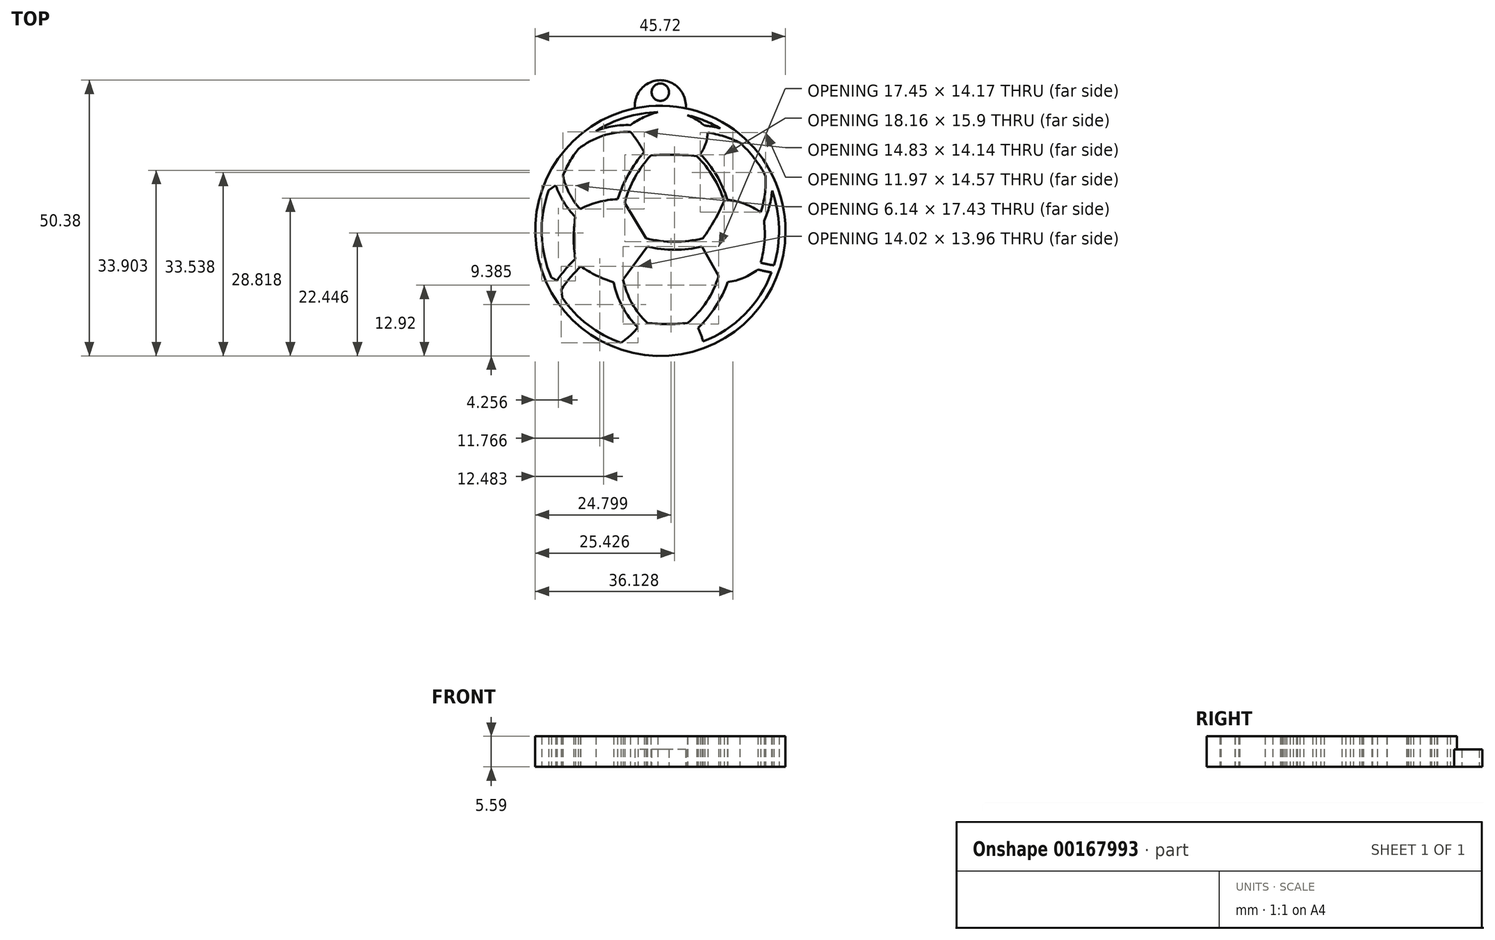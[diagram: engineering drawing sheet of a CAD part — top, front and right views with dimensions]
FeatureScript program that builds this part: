
annotation { "Feature Type Name" : "Feature", "Feature Type Description" : "" }
export const myFeature = defineFeature(function(context is Context, id is Id, definition is map)
    precondition{}
    {
        {
            var Q0;
            Q0=qCreatedBy(makeId("Top.planeOp"),FACE);
            var sketch = newSketch(context, id + "F0", { "sketchPlane" : qUnion([Q0])});
            skCircle(sketch, "E0", {"center": v(1.83, 6.23) * mm, "radius": 22.86 * mm});
            skPoint(sketch, "E0.centerSnap0", {"position": v(-21.03, 6.23) * mm});
            skPoint(sketch, "E0.centerSnap1", {"position": v(1.83, 29.1) * mm});
            skArc(sketch, "E1", {"start": v(9.64, -14) * mm, "mid": v(17.25, -9.02) * mm, "end": v(22.15, -1.36) * mm});
            skLineSegment(sketch, "E2", {"start": v(-18.54, 13.66) * mm, "end": v(-17.27, 14.53) * mm});
            skArc(sketch, "E3", {"start": v(-17.27, 14.53) * mm, "mid": v(-15.79, 11.46) * mm, "end": v(-13.7, 8.76) * mm});
            skArc(sketch, "E4", {"start": v(-13.15, 21.17) * mm, "mid": v(-14.73, 18.84) * mm, "end": v(-15.96, 16.3) * mm});
            skArc(sketch, "E5", {"start": v(-3.64, 25.54) * mm, "mid": v(-6.83, 25.35) * mm, "end": v(-9.9, 24.47) * mm});
            skArc(sketch, "E6", {"start": v(-3.64, 24.35) * mm, "mid": v(-8.67, 23.6) * mm, "end": v(-13.15, 21.17) * mm});
            skArc(sketch, "E7", {"start": v(-15.96, 16.3) * mm, "mid": v(-14.8, 13.05) * mm, "end": v(-12.82, 10.2) * mm});
            skArc(sketch, "E8", {"start": v(-5.97, 12.01) * mm, "mid": v(-9.5, 11.49) * mm, "end": v(-12.82, 10.2) * mm});
            skArc(sketch, "E9", {"start": v(-13.7, 8.76) * mm, "mid": v(-14, 4.92) * mm, "end": v(-13.7, 1.08) * mm});
            skArc(sketch, "E10", {"start": v(-13.7, 1.08) * mm, "mid": v(-15.51, -0.8) * mm, "end": v(-17.07, -2.9) * mm});
            skArc(sketch, "E11", {"start": v(-17.07, -2.9) * mm, "mid": v(-17.55, -2.57) * mm, "end": v(-18.08, -2.35) * mm});
            skArc(sketch, "E12", {"start": v(-16.1, -5.96) * mm, "mid": v(-16.15, -5.25) * mm, "end": v(-16.27, -4.55) * mm});
            skArc(sketch, "E13", {"start": v(-12.7, -0.26) * mm, "mid": v(-14.62, -2.3) * mm, "end": v(-16.27, -4.55) * mm});
            skArc(sketch, "E14", {"start": v(-12.7, -0.26) * mm, "mid": v(-9.8, -1.95) * mm, "end": v(-6.68, -3.16) * mm});
            skArc(sketch, "E15", {"start": v(-6.68, -3.16) * mm, "mid": v(-5.1, -7.64) * mm, "end": v(-2.25, -11.44) * mm});
            skArc(sketch, "E16", {"start": v(-5.37, -14.23) * mm, "mid": v(-3.72, -12.93) * mm, "end": v(-2.25, -11.44) * mm});
            skArc(sketch, "E17", {"start": v(-4.95, -2.65) * mm, "mid": v(-3.36, -6.97) * mm, "end": v(-0.54, -10.6) * mm});
            skArc(sketch, "E18", {"start": v(-0.54, -10.6) * mm, "mid": v(3.14, -10.8) * mm, "end": v(6.82, -10.6) * mm});
            skArc(sketch, "E19", {"start": v(6.82, -10.6) * mm, "mid": v(10.28, -6.74) * mm, "end": v(12.5, -2.04) * mm});
            skLineSegment(sketch, "E20", {"start": v(9.42, 3.37) * mm, "end": v(12.5, -2.04) * mm});
            skLineSegment(sketch, "E21", {"start": v(-4.95, -2.65) * mm, "end": v(-0.53, 3.38) * mm});
            skArc(sketch, "E22", {"start": v(-0.53, 3.38) * mm, "mid": v(4.44, 2.77) * mm, "end": v(9.42, 3.37) * mm});
            skLineSegment(sketch, "E23", {"start": v(-4.69, 11.3) * mm, "end": v(-0.81, 4.87) * mm});
            skArc(sketch, "E24", {"start": v(-0.81, 4.87) * mm, "mid": v(4.4, 4.24) * mm, "end": v(9.62, 4.87) * mm});
            skArc(sketch, "E25", {"start": v(9.62, 4.87) * mm, "mid": v(11.74, 8.16) * mm, "end": v(13.48, 11.67) * mm});
            skArc(sketch, "E26", {"start": v(13.48, 11.67) * mm, "mid": v(11.48, 16.08) * mm, "end": v(8.5, 19.9) * mm});
            skArc(sketch, "E27", {"start": v(0.08, 20) * mm, "mid": v(-2.84, 15.95) * mm, "end": v(-4.69, 11.3) * mm});
            skArc(sketch, "E28", {"start": v(8.5, 19.9) * mm, "mid": v(4.3, 20.14) * mm, "end": v(0.08, 20) * mm});
            skArc(sketch, "E29", {"start": v(-1.13, 20.62) * mm, "mid": v(-3.97, 16.55) * mm, "end": v(-5.97, 12.01) * mm});
            skArc(sketch, "E30", {"start": v(-1.13, 20.62) * mm, "mid": v(-2.3, 22.54) * mm, "end": v(-3.64, 24.35) * mm});
            skArc(sketch, "E31", {"start": v(1.38, 27.91) * mm, "mid": v(-1.25, 26.97) * mm, "end": v(-3.64, 25.54) * mm});
            skArc(sketch, "E32", {"start": v(9.95, 25.44) * mm, "mid": v(8.44, 26.51) * mm, "end": v(6.78, 27.35) * mm});
            skArc(sketch, "E33", {"start": v(12.8, 24.95) * mm, "mid": v(11.39, 25.28) * mm, "end": v(9.95, 25.44) * mm});
            skArc(sketch, "E34", {"start": v(16.36, 22.34) * mm, "mid": v(13.49, 23.48) * mm, "end": v(10.48, 24.2) * mm});
            skArc(sketch, "E35", {"start": v(9.11, 20.26) * mm, "mid": v(10.1, 22.12) * mm, "end": v(10.48, 24.2) * mm});
            skArc(sketch, "E36", {"start": v(14.05, 11.93) * mm, "mid": v(12.09, 16.4) * mm, "end": v(9.11, 20.26) * mm});
            skArc(sketch, "E37", {"start": v(20.17, 9.62) * mm, "mid": v(17.25, 11.14) * mm, "end": v(14.05, 11.93) * mm});
            skArc(sketch, "E38", {"start": v(20.17, 9.62) * mm, "mid": v(20.92, 12.9) * mm, "end": v(21.06, 16.27) * mm});
            skArc(sketch, "E39", {"start": v(20.78, 8.05) * mm, "mid": v(21.75, 10.74) * mm, "end": v(22.25, 13.56) * mm});
            skArc(sketch, "E40", {"start": v(20.17, 0.42) * mm, "mid": v(20.85, 4.2) * mm, "end": v(20.78, 8.05) * mm});
            skArc(sketch, "E41", {"start": v(20.17, 0.42) * mm, "mid": v(21.37, 0.12) * mm, "end": v(22.59, -0.06) * mm});
            skArc(sketch, "E42", {"start": v(19.63, -0.82) * mm, "mid": v(20.88, -1.13) * mm, "end": v(22.15, -1.36) * mm});
            skArc(sketch, "E43", {"start": v(14.16, -3.12) * mm, "mid": v(17.06, -2.36) * mm, "end": v(19.63, -0.82) * mm});
            skArc(sketch, "E44", {"start": v(8.72, -11.5) * mm, "mid": v(11.92, -7.62) * mm, "end": v(14.16, -3.12) * mm});
            skArc(sketch, "E45", {"start": v(9.64, -14) * mm, "mid": v(9.24, -12.73) * mm, "end": v(8.72, -11.5) * mm});
            skArc(sketch, "E46.trimOffspring", {"start": v(-16.1, -5.96) * mm, "mid": v(-11.4, -10.95) * mm, "end": v(-5.37, -14.23) * mm});
            skArc(sketch, "E47.trimOffspring", {"start": v(-18.54, 13.66) * mm, "mid": v(-19.84, 5.6) * mm, "end": v(-18.08, -2.35) * mm});
            skArc(sketch, "E48.trimOffspring", {"start": v(21.06, 16.27) * mm, "mid": v(18.98, 19.51) * mm, "end": v(16.36, 22.34) * mm});
            skArc(sketch, "E49.trimOffspring", {"start": v(22.59, -0.06) * mm, "mid": v(23.52, 6.78) * mm, "end": v(22.25, 13.56) * mm});
            skArc(sketch, "E50.trimOffspring", {"start": v(12.8, 24.95) * mm, "mid": v(9.88, 26.37) * mm, "end": v(6.78, 27.35) * mm});
            skArc(sketch, "E51.trimOffspring", {"start": v(1.38, 27.91) * mm, "mid": v(-4.5, 26.97) * mm, "end": v(-9.9, 24.47) * mm});
            skArc(sketch, "E52", {"start": v(6.47, 28.62) * mm, "mid": v(1.83, 33.75) * mm, "end": v(-2.8, 28.62) * mm});
            skCircle(sketch, "E53", {"center": v(1.83, 31.56) * mm, "radius": 1.59 * mm});
            skSolve(sketch);
        }
        {
            var Q0;
            Q0=makeQuery(id+"F0.imprint","IMPRINT",FACE,{"disambiguationData":[TD([[makeQuery(id+"F0.imprint","IMPRINT",EDGE,{"derivedFrom":sQuery(id+"F0.wireOp",EDGE,"E1")}),-1.0]])]});
            extrude(context, id + "F1", {"entities" : qUnion([Q0]), "depth" : 5.6 * mm});
        }
        {
            var Q0;
            {var subQ0=sQuery(id+"F0.wireOp",EDGE,"E52");Q0=makeQuery(id+"F0.imprint","IMPRINT",FACE,{"disambiguationData":[TD([[makeQuery(id+"F0.imprint","IMPRINT",EDGE,{"derivedFrom":subQ0}),1.0]])]});}
            extrude(context, id + "F2", {"entities" : qUnion([Q0]), "operationType" : NewBodyOperationType.ADD, "depth" : 3.17 * mm});
        }
    });
